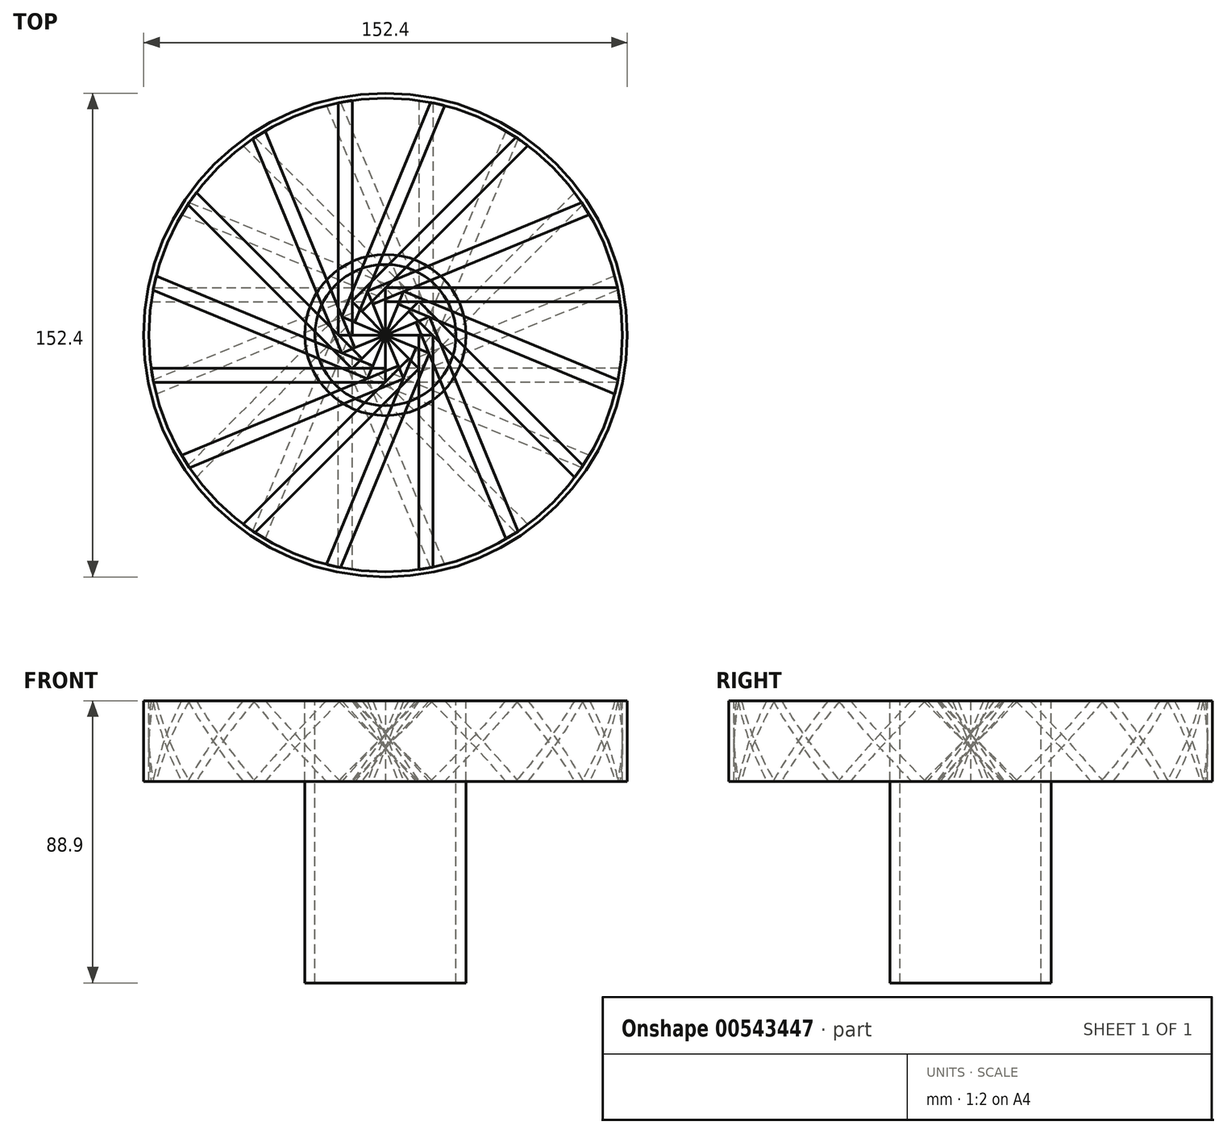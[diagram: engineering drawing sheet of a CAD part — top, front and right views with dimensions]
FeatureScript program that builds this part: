
annotation { "Feature Type Name" : "Feature", "Feature Type Description" : "" }
export const myFeature = defineFeature(function(context is Context, id is Id, definition is map)
    precondition{}
    {
        {
            var Q0;
            Q0=qCreatedBy(makeId("Top.planeOp"),FACE);
            var sketch = newSketch(context, id + "F0", { "sketchPlane" : qUnion([Q0])});
            skCircle(sketch, "E0", {"center": v(0, 0) * mm, "radius": 22.23 * mm});
            skCircle(sketch, "E1", {"center": v(0, 0) * mm, "radius": 25.4 * mm});
            skSolve(sketch);
        }
        {
            var Q0;
            Q0=makeQuery(id+"F0.imprint","IMPRINT",FACE,{"disambiguationData":[TD([[makeQuery(id+"F0.imprint","IMPRINT",EDGE,{"derivedFrom":sQuery(id+"F0.wireOp",EDGE,"E0")}),-1.0]])]});
            extrude(context, id + "F1", {"entities" : qUnion([Q0]), "oppositeDirection" : true, "depth" : 88.9 * mm, "offsetDistance" : 25.4 * mm});
        }
        {
            var Q0;
            Q0=qCreatedBy(makeId("Top.planeOp"),FACE);
            var sketch = newSketch(context, id + "F2", { "sketchPlane" : qUnion([Q0])});
            skCircle(sketch, "E2", {"center": v(0, 0) * mm, "radius": 76.2 * mm});
            skCircle(sketch, "E3", {"center": v(0, 0) * mm, "radius": 74.61 * mm});
            skSolve(sketch);
        }
        {
            var Q0;
            Q0=makeQuery(id+"F2.imprint","IMPRINT",FACE,{"disambiguationData":[TD([[makeQuery(id+"F2.imprint","IMPRINT",EDGE,{"derivedFrom":sQuery(id+"F2.wireOp",EDGE,"E2")}),1.0]])]});
            extrude(context, id + "F3", {"entities" : qUnion([Q0]), "oppositeDirection" : true, "depth" : 25.4 * mm, "offsetDistance" : 25.4 * mm});
        }
        {
            var Q0;
            Q0=qCreatedBy(makeId("Front.planeOp"),FACE);
            var sketch = newSketch(context, id + "F4", { "sketchPlane" : qUnion([Q0])});
            skLineSegment(sketch, "E4.0", {"start": v(-76.2, -25.4) * mm, "end": v(76.2, -25.4) * mm});
            skLineSegment(sketch, "E5.0", {"start": v(-76.2, 0) * mm, "end": v(76.2, 0) * mm});
            skLineSegment(sketch, "E6.0", {"start": v(10.45, 0) * mm, "end": v(-13.82, -24.28) * mm});
            skLineSegment(sketch, "E7.0", {"start": v(13.82, -1.12) * mm, "end": v(-10.45, -25.4) * mm});
            skLineSegment(sketch, "E8", {"start": v(-13.82, -24.28) * mm, "end": v(-14.95, -25.4) * mm});
            skLineSegment(sketch, "E9", {"start": v(-14.95, -25.4) * mm, "end": v(-10.45, -25.4) * mm});
            skLineSegment(sketch, "E10", {"start": v(13.82, -1.12) * mm, "end": v(14.95, 0) * mm});
            skLineSegment(sketch, "E11", {"start": v(14.95, 0) * mm, "end": v(10.45, 0) * mm});
            skSolve(sketch);
        }
        {
            var Q0;
            Q0=makeQuery(id+"F4.imprint","IMPRINT",FACE,{"disambiguationData":[TD([[makeQuery(id+"F4.imprint","IMPRINT",EDGE,{"derivedFrom":sQuery(id+"F4.wireOp",EDGE,"E6.0")}),1.0]])]});
            var Q1;
            Q1=makeQuery(id+"F3.opExtrude","SWEPT_FACE",FACE,{"disambiguationData":[OSD([sQuery(id+"F2.wireOp",EDGE,"E3")])]});
            extrude(context, id + "F5", {"entities" : qUnion([Q0]), "endBound" : BoundingType.UP_TO_SURFACE, "depth" : 25.4 * mm, "endBoundEntityFace" : qUnion([Q1]), "offsetDistance" : 25.4 * mm});
        }
        {
            var Q0;
            Q0=makeQuery(id+"F1.opExtrude","SWEPT_BODY",BODY,{"disambiguationData":[OSD([sQuery(id+"F0.wireOp",EDGE,"E0"),sQuery(id+"F0.wireOp",EDGE,"E1")])]});
            var Q1;
            Q1=makeQuery(id+"F5.opExtrude","SWEPT_BODY",BODY,{"disambiguationData":[OSD([sQuery(id+"F4.wireOp",EDGE,"E6.0"),sQuery(id+"F4.wireOp",EDGE,"E7.0"),sQuery(id+"F4.wireOp",EDGE,"E8"),sQuery(id+"F4.wireOp",EDGE,"E9"),sQuery(id+"F4.wireOp",EDGE,"E10"),sQuery(id+"F4.wireOp",EDGE,"E11")])]});
            var Q2;
            Q2=makeQuery(id+"F1.opExtrude","SWEPT_FACE",FACE,{"disambiguationData":[OSD([sQuery(id+"F0.wireOp",EDGE,"E0")])]});
            circularPattern(context, id + "F6", {"entities" : qUnion([Q0, Q1]), "axis" : qUnion([Q2]), "angle" : 360 * degree, "instanceCount" : 16, "equalSpace" : true});
        }
    });
